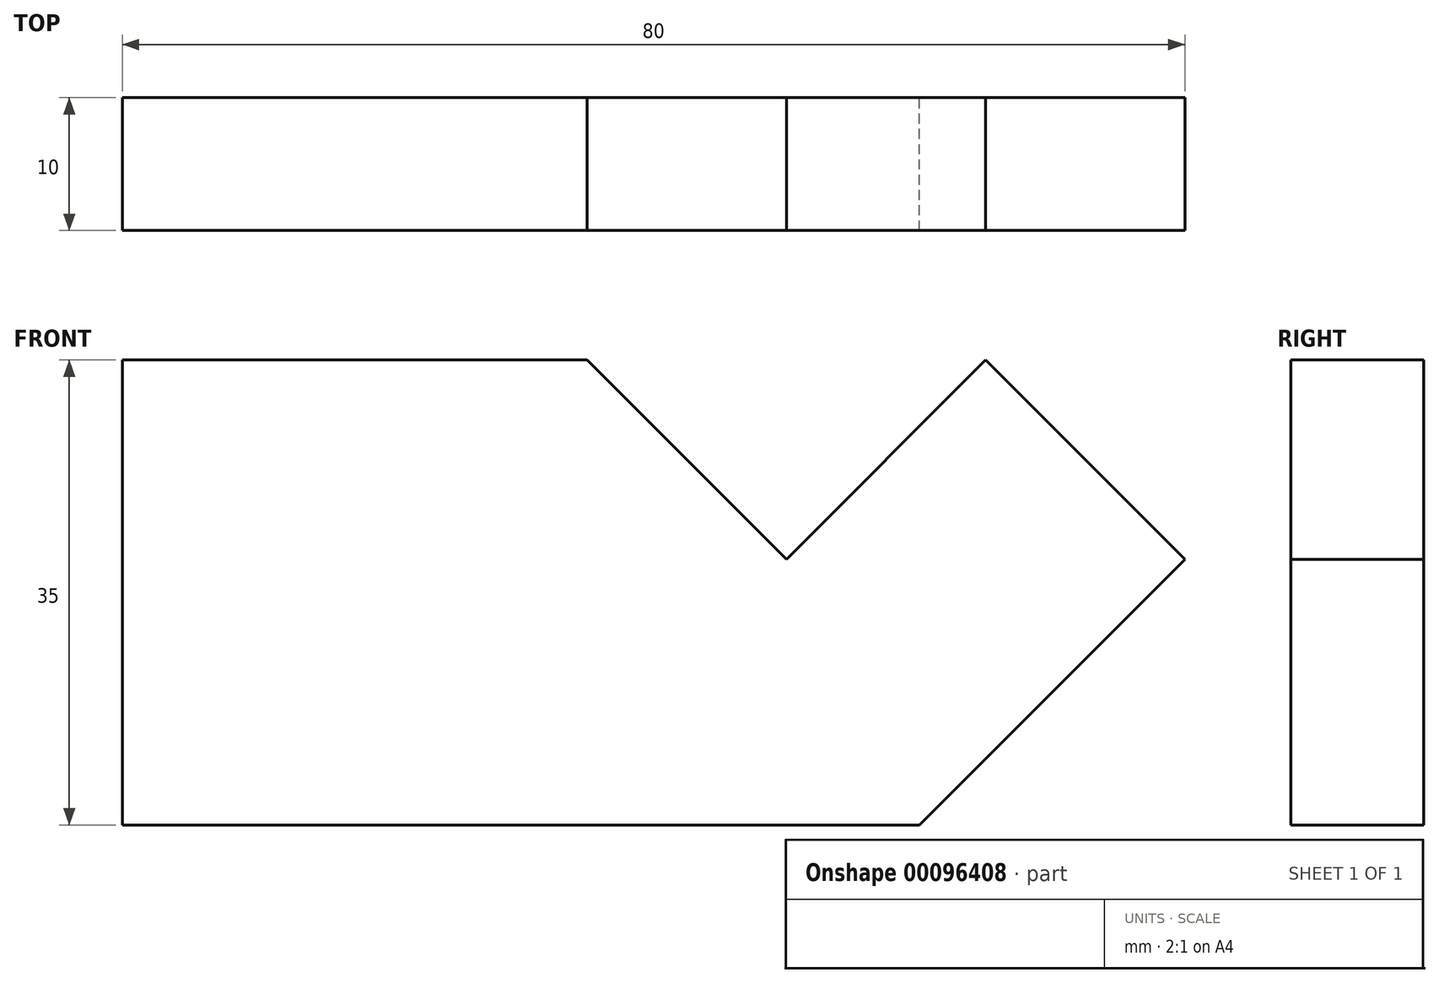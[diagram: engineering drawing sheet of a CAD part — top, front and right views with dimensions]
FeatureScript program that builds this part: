
annotation { "Feature Type Name" : "Feature", "Feature Type Description" : "" }
export const myFeature = defineFeature(function(context is Context, id is Id, definition is map)
    precondition{}
    {
        {
            var Q0;
            Q0=qCreatedBy(makeId("Front.planeOp"),FACE);
            var sketch = newSketch(context, id + "F0", { "sketchPlane" : qUnion([Q0])});
            skLineSegment(sketch, "E0", {"start": v(0, 0) * mm, "end": v(60, 0) * mm});
            skLineSegment(sketch, "E1", {"start": v(60, 0) * mm, "end": v(80, 20) * mm});
            skLineSegment(sketch, "E2", {"start": v(80, 20) * mm, "end": v(65, 35) * mm});
            skLineSegment(sketch, "E3", {"start": v(65, 35) * mm, "end": v(50, 20) * mm});
            skLineSegment(sketch, "E4", {"start": v(50, 20) * mm, "end": v(35, 35) * mm});
            skLineSegment(sketch, "E5", {"start": v(35, 35) * mm, "end": v(0, 35) * mm});
            skLineSegment(sketch, "E6", {"start": v(0, 35) * mm, "end": v(0, 0) * mm});
            skLineSegment(sketch, "E7", {"start": v(35, 35) * mm, "end": v(65, 35) * mm, "construction": true});
            skSolve(sketch);
        }
        {
            var Q0;
            Q0=makeQuery(id+"F0.imprint","IMPRINT",FACE,{"disambiguationData":[TD([[makeQuery(id+"F0.imprint","IMPRINT",EDGE,{"derivedFrom":sQuery(id+"F0.wireOp",EDGE,"E0")}),1.0]])]});
            extrude(context, id + "F1", {"entities" : qUnion([Q0]), "depth" : 10 * mm});
        }
    });
